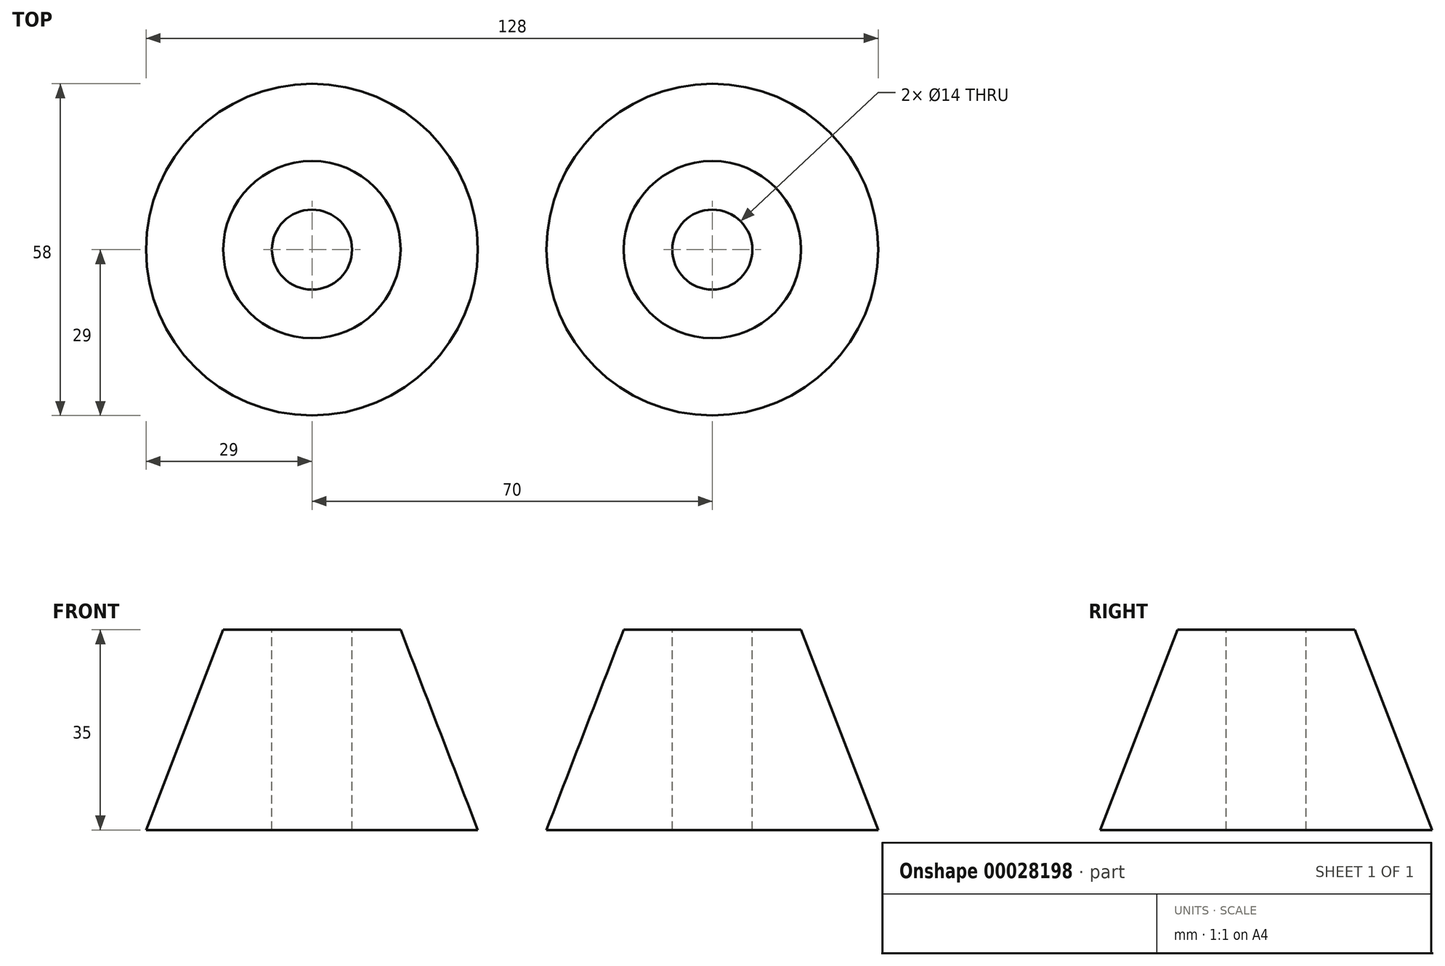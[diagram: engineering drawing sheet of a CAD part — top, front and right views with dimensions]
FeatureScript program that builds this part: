
annotation { "Feature Type Name" : "Feature", "Feature Type Description" : "" }
export const myFeature = defineFeature(function(context is Context, id is Id, definition is map)
    precondition{}
    {
        {
            var Q0;
            Q0=qCreatedBy(makeId("Top.planeOp"),FACE);
            var sketch = newSketch(context, id + "F0", { "sketchPlane" : qUnion([Q0])});
            skCircle(sketch, "E0", {"center": v(0, 0) * mm, "radius": 29 * mm});
            skSolve(sketch);
        }
        {
            var Q0;
            Q0=qCreatedBy(makeId("Top.planeOp"),FACE);
            cPlane(context, id + "F1", {"entities" : qUnion([Q0]), "cplaneType" : CPlaneType.OFFSET, "offset" : 35 * mm, "width" : 150 * mm, "height" : 150 * mm});
        }
        {
            var Q0;
            Q0=qCreatedBy(id+"F1.planeOp",FACE);
            var sketch = newSketch(context, id + "F2", { "sketchPlane" : qUnion([Q0])});
            skCircle(sketch, "E1", {"center": v(0, 0) * mm, "radius": 15.5 * mm});
            skSolve(sketch);
        }
        {
            var Q0;
            Q0=makeQuery(id+"F0.imprint","IMPRINT",FACE,{"disambiguationData":[TD([[makeQuery(id+"F0.imprint","IMPRINT",EDGE,{"derivedFrom":sQuery(id+"F0.wireOp",EDGE,"E0")}),1.0]])]});
            var Q1;
            Q1=makeQuery(id+"F2.imprint","IMPRINT",FACE,{"disambiguationData":[TD([[makeQuery(id+"F2.imprint","IMPRINT",EDGE,{"derivedFrom":sQuery(id+"F2.wireOp",EDGE,"E1")}),1.0]])]});
            loft(context, id + "F3", {"sheetProfilesArray" : [{ "sheetProfileEntities" : qUnion([Q0]) }, { "sheetProfileEntities" : qUnion([Q1]) }]});
        }
        {
            var Q0;
            Q0=makeQuery(id+"F3.opLoft","CAP_FACE",FACE,{"disambiguationData":[OSD([makeQuery(id+"F2.imprint","IMPRINT",FACE,{"disambiguationData":[TD([[makeQuery(id+"F2.imprint","IMPRINT",EDGE,{"derivedFrom":sQuery(id+"F2.wireOp",EDGE,"E1")}),1.0]])]})])],"isStart":true});
            var sketch = newSketch(context, id + "F4", { "sketchPlane" : qUnion([Q0])});
            skCircle(sketch, "E2", {"center": v(0, 0) * mm, "radius": 7 * mm});
            skSolve(sketch);
        }
        {
            var Q0;
            Q0=makeQuery(id+"F4.imprint","IMPRINT",FACE,{"disambiguationData":[TD([[makeQuery(id+"F4.imprint","IMPRINT",EDGE,{"derivedFrom":sQuery(id+"F4.wireOp",EDGE,"E2")}),1.0]])]});
            extrude(context, id + "F5", {"entities" : qUnion([Q0]), "operationType" : NewBodyOperationType.REMOVE, "endBound" : BoundingType.THROUGH_ALL, "oppositeDirection" : true, "depth" : 25 * mm});
        }
        {
            var Q0;
            Q0=qCreatedBy(makeId("Right.planeOp"),FACE);
            cPlane(context, id + "F6", {"entities" : qUnion([Q0]), "cplaneType" : CPlaneType.OFFSET, "offset" : 35 * mm, "width" : 150 * mm, "height" : 150 * mm});
        }
        {
            var Q0;
            Q0=makeQuery(id+"F3.opLoft","SWEPT_BODY",BODY,{"disambiguationData":[OSD([makeQuery(id+"F0.imprint","IMPRINT",FACE,{"disambiguationData":[TD([[makeQuery(id+"F0.imprint","IMPRINT",EDGE,{"derivedFrom":sQuery(id+"F0.wireOp",EDGE,"E0")}),1.0]])]}),makeQuery(id+"F2.imprint","IMPRINT",FACE,{"disambiguationData":[TD([[makeQuery(id+"F2.imprint","IMPRINT",EDGE,{"derivedFrom":sQuery(id+"F2.wireOp",EDGE,"E1")}),1.0]])]})])]});
            var Q1;
            Q1=qCreatedBy(id+"F6.planeOp",FACE);
            mirror(context, id + "F7", {"entities" : qUnion([Q0]), "mirrorPlane" : qUnion([Q1])});
        }
    });
